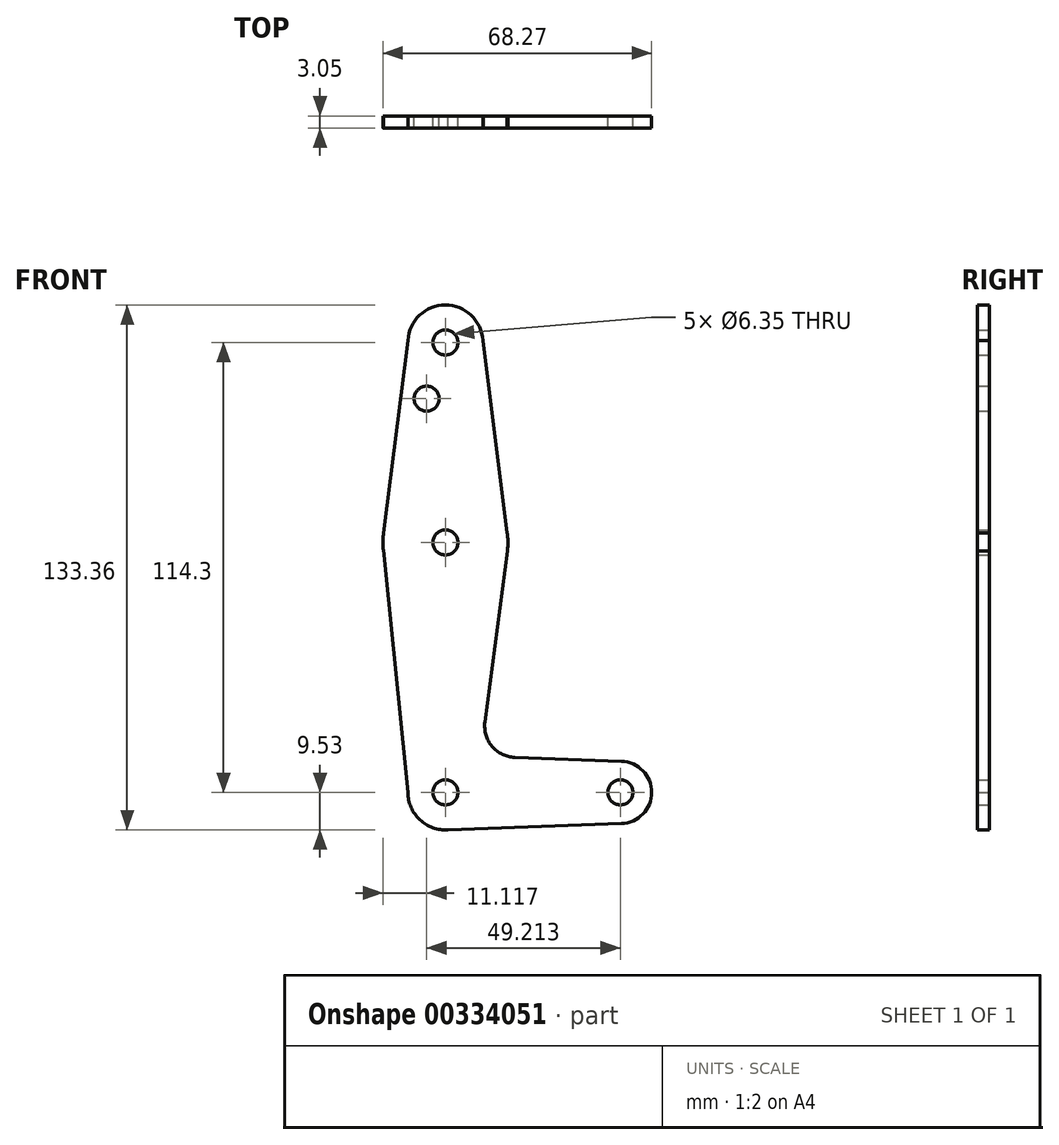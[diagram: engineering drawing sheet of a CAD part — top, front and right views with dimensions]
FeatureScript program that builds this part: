
annotation { "Feature Type Name" : "Feature", "Feature Type Description" : "" }
export const myFeature = defineFeature(function(context is Context, id is Id, definition is map)
    precondition{}
    {
        {
            var Q0;
            Q0=qCreatedBy(makeId("Front.planeOp"),FACE);
            var sketch = newSketch(context, id + "F0", { "sketchPlane" : qUnion([Q0])});
            skLineSegment(sketch, "E0", {"start": v(0, 114.3) * mm, "end": v(0, 0) * mm, "construction": true});
            skLineSegment(sketch, "E1", {"start": v(0, 0) * mm, "end": v(44.45, 0) * mm, "construction": true});
            skCircle(sketch, "E2", {"center": v(0, 114.3) * mm, "radius": 9.53 * mm});
            skCircle(sketch, "E3", {"center": v(0, 0) * mm, "radius": 9.53 * mm});
            skCircle(sketch, "E4", {"center": v(44.45, 0) * mm, "radius": 7.94 * mm});
            skCircle(sketch, "E5", {"center": v(0, 63.5) * mm, "radius": 15.88 * mm});
            skCircle(sketch, "E6", {"center": v(0, 114.3) * mm, "radius": 3.18 * mm});
            skCircle(sketch, "E7", {"center": v(0, 63.5) * mm, "radius": 3.18 * mm});
            skCircle(sketch, "E8", {"center": v(0, 0) * mm, "radius": 3.18 * mm});
            skCircle(sketch, "E9", {"center": v(44.45, 0) * mm, "radius": 3.18 * mm});
            skLineSegment(sketch, "E10", {"start": v(17.64, 8.9) * mm, "end": v(44.73, 7.93) * mm});
            skLineSegment(sketch, "E11", {"start": v(0, -9.53) * mm, "end": v(44.73, -7.93) * mm});
            skCircle(sketch, "E12", {"center": v(-4.76, 100.03) * mm, "radius": 3.18 * mm});
            skLineSegment(sketch, "E13", {"start": v(15.76, 61.6) * mm, "end": v(10.04, 17.87) * mm});
            skLineSegment(sketch, "E14", {"start": v(-15.76, 61.6) * mm, "end": v(-9.52, 0) * mm});
            skArc(sketch, "E15.filletArc", {"start": v(10.04, 17.87) * mm, "mid": v(11.85, 11.7) * mm, "end": v(17.64, 8.9) * mm});
            skLineSegment(sketch, "E16", {"start": v(-15.8, 65.04) * mm, "end": v(-9.5, 114.83) * mm});
            skLineSegment(sketch, "E17", {"start": v(9.5, 114.83) * mm, "end": v(15.8, 65.04) * mm});
            skSolve(sketch);
        }
        {
            var Q0;
            Q0 = qSketchRegion(id + "F0", true);
            extrude(context, id + "F1", {"entities" : qUnion([Q0]), "depth" : 3.05 * mm});
        }
    });
